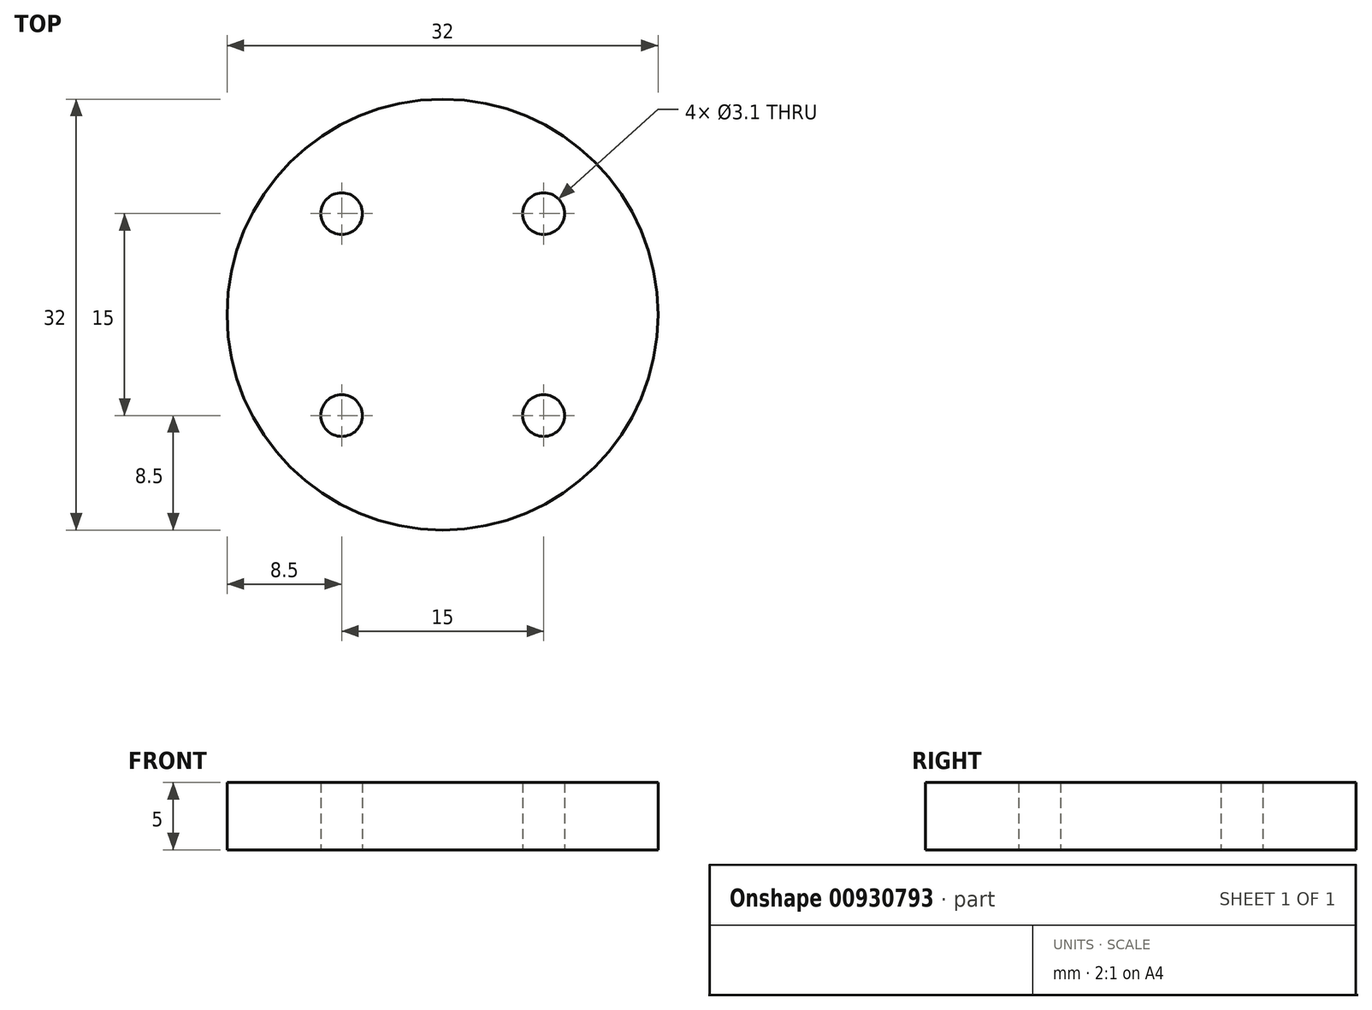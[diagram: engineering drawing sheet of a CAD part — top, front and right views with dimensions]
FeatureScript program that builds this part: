
annotation { "Feature Type Name" : "Feature", "Feature Type Description" : "" }
export const myFeature = defineFeature(function(context is Context, id is Id, definition is map)
    precondition{}
    {
        {
            var Q0;
            Q0=qCreatedBy(makeId("Top.planeOp"),FACE);
            var sketch = newSketch(context, id + "F0", { "sketchPlane" : qUnion([Q0])});
            skCircle(sketch, "E0", {"center": v(0, 0) * mm, "radius": 16 * mm});
            skLineSegment(sketch, "E1.bottom", {"start": v(7.5, -7.5) * mm, "end": v(-7.5, -7.5) * mm});
            skLineSegment(sketch, "E1.top", {"start": v(7.5, 7.5) * mm, "end": v(-7.5, 7.5) * mm});
            skLineSegment(sketch, "E1.left", {"start": v(7.5, -7.5) * mm, "end": v(7.5, 7.5) * mm});
            skLineSegment(sketch, "E1.right", {"start": v(-7.5, -7.5) * mm, "end": v(-7.5, 7.5) * mm});
            skCircle(sketch, "E2", {"center": v(-7.5, 7.5) * mm, "radius": 1.55 * mm});
            skCircle(sketch, "E3", {"center": v(7.5, 7.5) * mm, "radius": 1.55 * mm});
            skCircle(sketch, "E4", {"center": v(7.5, -7.5) * mm, "radius": 1.55 * mm});
            skCircle(sketch, "E5", {"center": v(-7.5, -7.5) * mm, "radius": 1.55 * mm});
            skSolve(sketch);
        }
        {
            var Q0;
            Q0=makeQuery(id+"F0.imprint","IMPRINT",FACE,{"disambiguationData":[TD([[makeQuery(id+"F0.imprint","IMPRINT",EDGE,{"derivedFrom":sQuery(id+"F0.wireOp",EDGE,"E0")}),1.0]])]});
            var Q1;
            {var subQ5=sQuery(id+"F0.wireOp",EDGE,"E4");var subQ10=sQuery(id+"F0.wireOp",EDGE,"E1.bottom");var subQ15=makeQuery(id+"F0.imprint","INTERSECT",VERTEX,{"derivedFrom":[subQ10,subQ5]});Q1=makeQuery(id+"F0.imprint","IMPRINT",FACE,{"disambiguationData":[TD([[makeQuery(id+"F0.imprint","IMPRINT",EDGE,{"disambiguationData":[TD([[subQ15,-1.0]])],"derivedFrom":subQ10}),-1.0]])]});}
            extrude(context, id + "F1", {"entities" : qUnion([Q0, Q1]), "depth" : 5 * mm, "offsetDistance" : 25 * mm});
        }
    });
